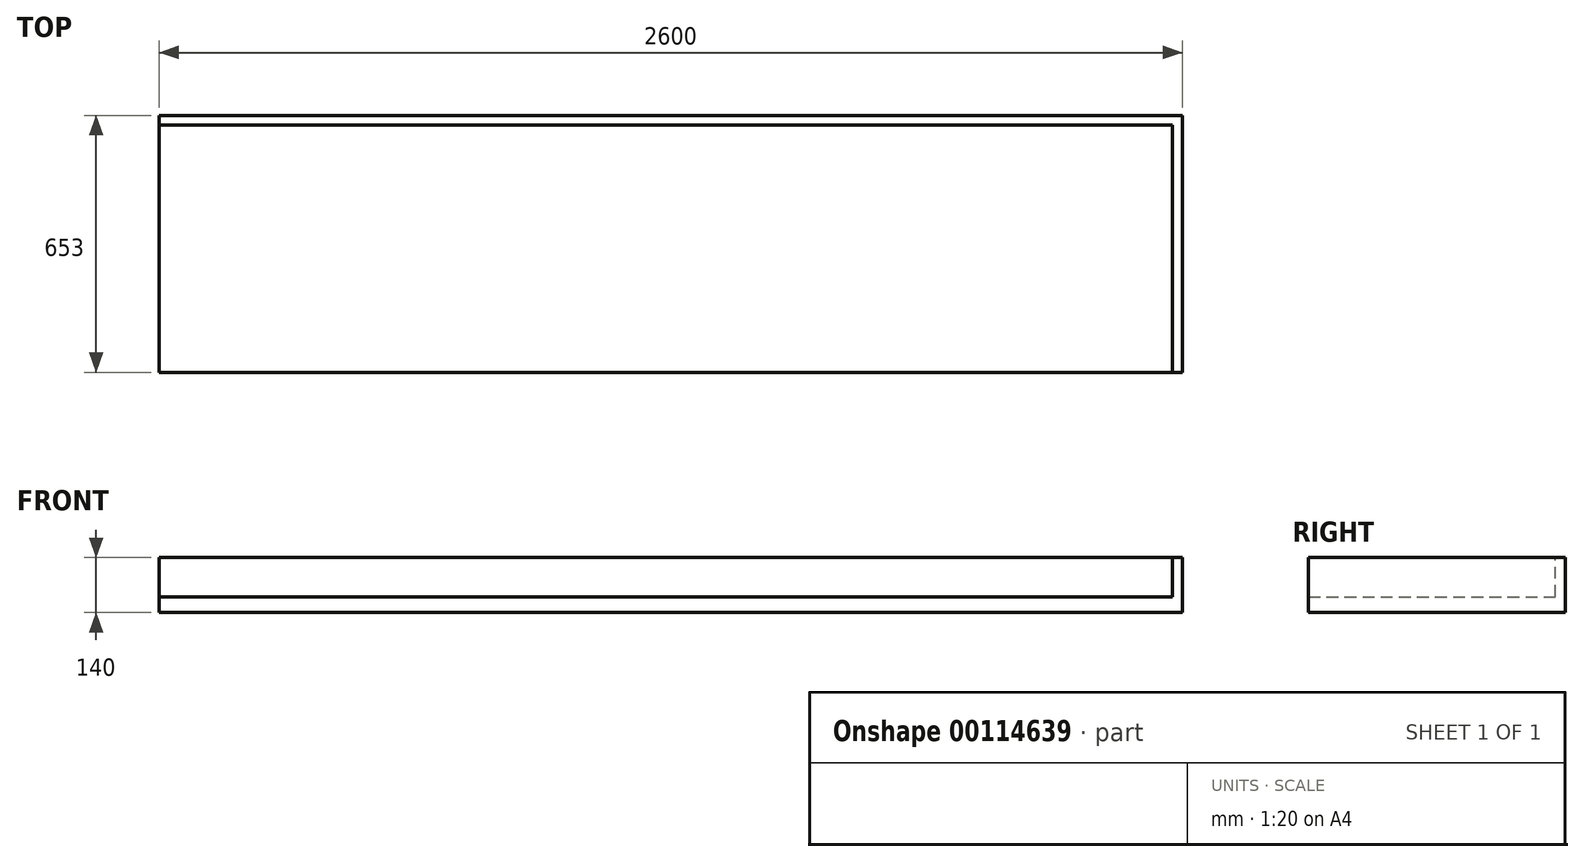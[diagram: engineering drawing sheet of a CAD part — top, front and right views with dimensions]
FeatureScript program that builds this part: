
annotation { "Feature Type Name" : "Feature", "Feature Type Description" : "" }
export const myFeature = defineFeature(function(context is Context, id is Id, definition is map)
    precondition{}
    {
        {
            var Q0;
            Q0=qCreatedBy(makeId("Front.planeOp"),FACE);
            var sketch = newSketch(context, id + "F0", { "sketchPlane" : qUnion([Q0])});
            skLineSegment(sketch, "E0.bottom", {"start": v(1287.5, -20) * mm, "end": v(-1287.5, -20) * mm});
            skLineSegment(sketch, "E0.top", {"start": v(1287.5, 20) * mm, "end": v(-1287.5, 20) * mm});
            skLineSegment(sketch, "E0.left", {"start": v(1287.5, -20) * mm, "end": v(1287.5, 20) * mm});
            skLineSegment(sketch, "E0.right", {"start": v(-1287.5, -20) * mm, "end": v(-1287.5, 20) * mm});
            skPoint(sketch, "E0.middle", {"position": v(0, 0) * mm});
            skSolve(sketch);
        }
        {
            var Q0;
            Q0=makeQuery(id+"F0.imprint","IMPRINT",FACE,{"disambiguationData":[TD([[makeQuery(id+"F0.imprint","IMPRINT",EDGE,{"derivedFrom":sQuery(id+"F0.wireOp",EDGE,"E0.bottom")}),-1.0]])]});
            extrude(context, id + "F1", {"entities" : qUnion([Q0]), "depth" : 628 * mm});
        }
        {
            var Q0;
            Q0=makeQuery(id+"F1.opExtrude","CAP_FACE",FACE,{"disambiguationData":[OSD([sQuery(id+"F0.wireOp",EDGE,"E0.bottom"),sQuery(id+"F0.wireOp",EDGE,"E0.top"),sQuery(id+"F0.wireOp",EDGE,"E0.left"),sQuery(id+"F0.wireOp",EDGE,"E0.right")])],"isStart":true});
            var sketch = newSketch(context, id + "F2", { "sketchPlane" : qUnion([Q0])});
            skLineSegment(sketch, "E1.bottom", {"start": v(1287.5, -20) * mm, "end": v(-1287.5, -20) * mm});
            skLineSegment(sketch, "E1.top", {"start": v(1287.5, 120) * mm, "end": v(-1287.5, 120) * mm});
            skLineSegment(sketch, "E1.left", {"start": v(1287.5, -20) * mm, "end": v(1287.5, 120) * mm});
            skLineSegment(sketch, "E1.right", {"start": v(-1287.5, -20) * mm, "end": v(-1287.5, 120) * mm});
            skSolve(sketch);
        }
        {
            var Q0;
            Q0 = qSketchRegion(id + "F2", true);
            extrude(context, id + "F3", {"entities" : qUnion([Q0]), "operationType" : NewBodyOperationType.ADD, "depth" : 25 * mm});
        }
        {
            var Q0;
            Q0=makeQuery(id+"F3.boolean.opBoolean","MERGE",FACE,{"derivedFrom":[makeQuery(id+"F1.opExtrude","SWEPT_FACE",FACE,{"disambiguationData":[OSD([sQuery(id+"F0.wireOp",EDGE,"E0.left")])]}),makeQuery(id+"F3.opExtrude","SWEPT_FACE",FACE,{"disambiguationData":[OSD([sQuery(id+"F2.wireOp",EDGE,"E1.right")])]})]});
            var sketch = newSketch(context, id + "F4", { "sketchPlane" : qUnion([Q0])});
            skLineSegment(sketch, "E2.bottom", {"start": v(-628, -20) * mm, "end": v(25, -20) * mm});
            skLineSegment(sketch, "E2.top", {"start": v(-628, 120) * mm, "end": v(25, 120) * mm});
            skLineSegment(sketch, "E2.left", {"start": v(-628, -20) * mm, "end": v(-628, 120) * mm});
            skLineSegment(sketch, "E2.right", {"start": v(25, -20) * mm, "end": v(25, 120) * mm});
            skSolve(sketch);
        }
        {
            var Q0;
            Q0 = qSketchRegion(id + "F4", true);
            extrude(context, id + "F5", {"entities" : qUnion([Q0]), "operationType" : NewBodyOperationType.ADD, "depth" : 25 * mm});
        }
    });
